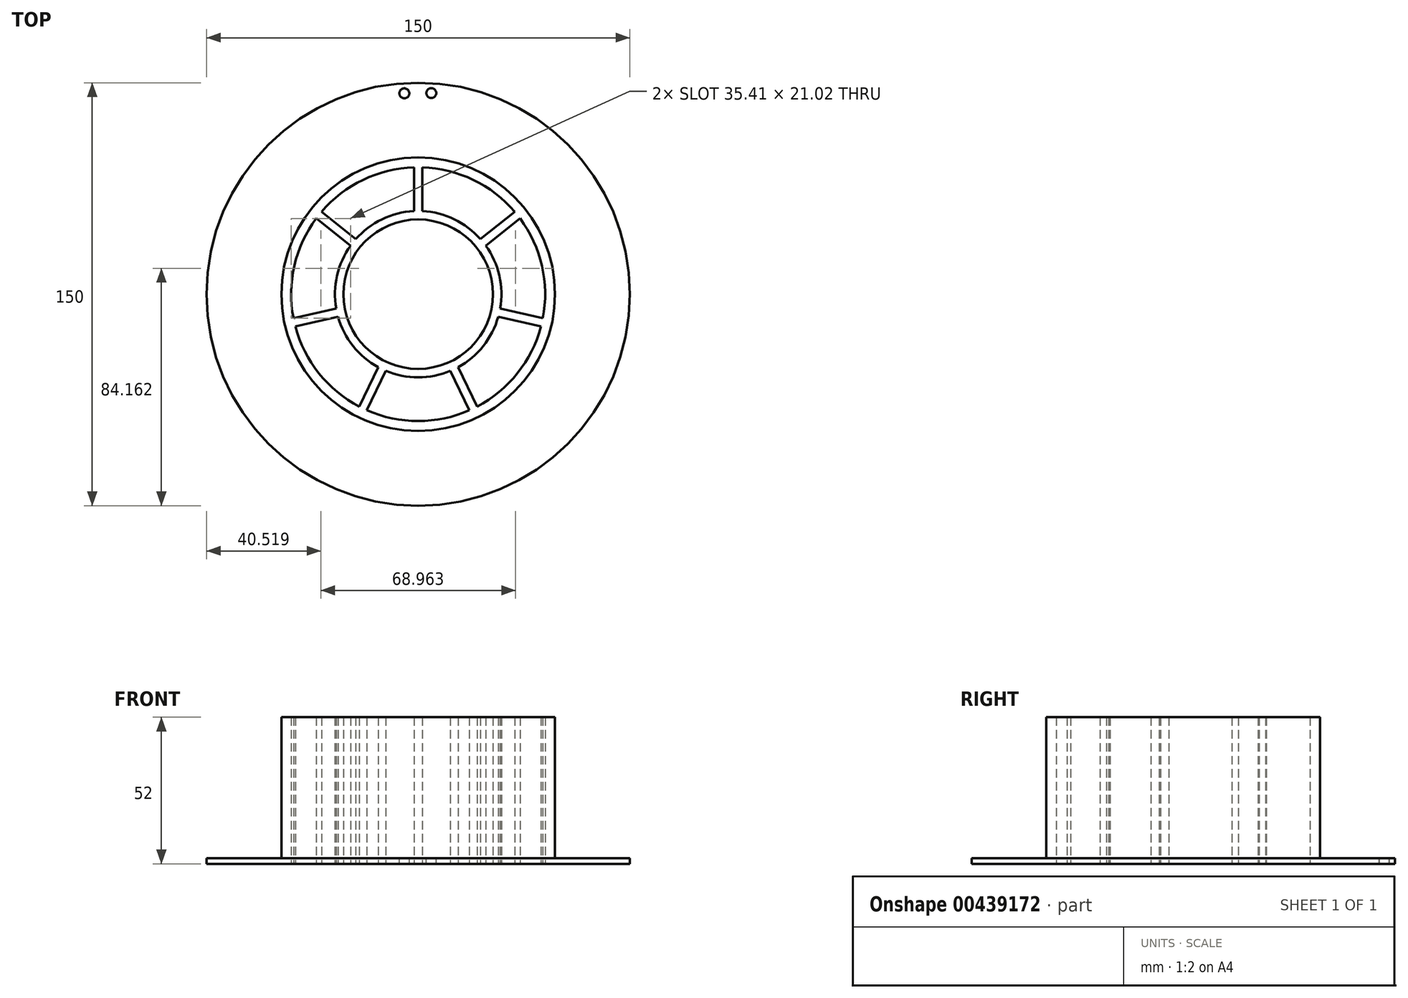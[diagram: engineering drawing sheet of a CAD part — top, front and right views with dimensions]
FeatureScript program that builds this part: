
annotation { "Feature Type Name" : "Feature", "Feature Type Description" : "" }
export const myFeature = defineFeature(function(context is Context, id is Id, definition is map)
    precondition{}
    {
        {
            var Q0;
            Q0=qCreatedBy(makeId("Top.planeOp"),FACE);
            var sketch = newSketch(context, id + "F0", { "sketchPlane" : qUnion([Q0])});
            skCircle(sketch, "E0", {"center": v(0, 0) * mm, "radius": 26.5 * mm});
            skArc(sketch, "E1", {"start": v(-1.5, 29.46) * mm, "mid": v(-12.8, 26.58) * mm, "end": v(-22.1, 19.54) * mm});
            skArc(sketch, "E2", {"start": v(-1.5, 44.97) * mm, "mid": v(-19.52, 40.54) * mm, "end": v(-34.23, 29.21) * mm});
            skCircle(sketch, "E3", {"center": v(0, 0) * mm, "radius": 75 * mm});
            skLineSegment(sketch, "E4", {"start": v(-1.5, 29.46) * mm, "end": v(-1.5, 44.97) * mm});
            skLineSegment(sketch, "E5", {"start": v(1.5, 29.46) * mm, "end": v(1.5, 44.97) * mm});
            skLineSegment(sketch, "E6.1.0", {"start": v(-23.97, 17.2) * mm, "end": v(-36.1, 26.87) * mm});
            skLineSegment(sketch, "E6.1.1", {"start": v(-22.1, 19.54) * mm, "end": v(-34.23, 29.21) * mm});
            skLineSegment(sketch, "E6.2.0", {"start": v(-28.39, -8.02) * mm, "end": v(-43.51, -11.47) * mm});
            skLineSegment(sketch, "E6.2.1", {"start": v(-29.06, -5.1) * mm, "end": v(-44.18, -8.55) * mm});
            skLineSegment(sketch, "E6.3.0", {"start": v(-11.43, -27.2) * mm, "end": v(-18.16, -41.17) * mm});
            skLineSegment(sketch, "E6.3.1", {"start": v(-14.13, -25.9) * mm, "end": v(-20.87, -39.87) * mm});
            skLineSegment(sketch, "E6.4.0", {"start": v(14.13, -25.9) * mm, "end": v(20.87, -39.87) * mm});
            skLineSegment(sketch, "E6.4.1", {"start": v(11.43, -27.2) * mm, "end": v(18.16, -41.17) * mm});
            skLineSegment(sketch, "E6.5.0", {"start": v(29.06, -5.1) * mm, "end": v(44.18, -8.55) * mm});
            skLineSegment(sketch, "E6.5.1", {"start": v(28.39, -8.02) * mm, "end": v(43.51, -11.47) * mm});
            skLineSegment(sketch, "E6.6.0", {"start": v(22.1, 19.54) * mm, "end": v(34.23, 29.21) * mm});
            skLineSegment(sketch, "E6.6.1", {"start": v(23.97, 17.2) * mm, "end": v(36.1, 26.87) * mm});
            skLineSegment(sketch, "E6.anchor1", {"start": v(0, 0) * mm, "end": v(-1.5, 29.46) * mm, "construction": true});
            skLineSegment(sketch, "E6.anchor2", {"start": v(0, 0) * mm, "end": v(-1.5, 29.46) * mm, "construction": true});
            skArc(sketch, "E7.trimOffspring", {"start": v(-36.1, 26.87) * mm, "mid": v(-43.87, 10.01) * mm, "end": v(-44.18, -8.55) * mm});
            skArc(sketch, "E8.trimOffspring", {"start": v(-23.97, 17.2) * mm, "mid": v(-28.76, 6.56) * mm, "end": v(-29.06, -5.1) * mm});
            skArc(sketch, "E9.trimOffspring", {"start": v(-28.39, -8.02) * mm, "mid": v(-23.06, -18.4) * mm, "end": v(-14.13, -25.9) * mm});
            skArc(sketch, "E10.trimOffspring", {"start": v(-43.51, -11.47) * mm, "mid": v(-35.18, -28.06) * mm, "end": v(-20.87, -39.87) * mm});
            skArc(sketch, "E11.trimOffspring", {"start": v(-11.43, -27.2) * mm, "mid": v(0, -29.5) * mm, "end": v(11.43, -27.2) * mm});
            skArc(sketch, "E12.trimOffspring", {"start": v(-18.16, -41.17) * mm, "mid": v(0, -45) * mm, "end": v(18.16, -41.17) * mm});
            skArc(sketch, "E13.trimOffspring", {"start": v(14.13, -25.9) * mm, "mid": v(23.06, -18.4) * mm, "end": v(28.39, -8.02) * mm});
            skArc(sketch, "E14.trimOffspring", {"start": v(20.87, -39.87) * mm, "mid": v(35.18, -28.06) * mm, "end": v(43.51, -11.47) * mm});
            skArc(sketch, "E15.trimOffspring", {"start": v(44.18, -8.55) * mm, "mid": v(43.87, 10.01) * mm, "end": v(36.1, 26.87) * mm});
            skArc(sketch, "E16.trimOffspring", {"start": v(29.06, -5.1) * mm, "mid": v(28.76, 6.56) * mm, "end": v(23.97, 17.2) * mm});
            skArc(sketch, "E17.trimOffspring", {"start": v(34.23, 29.21) * mm, "mid": v(19.52, 40.54) * mm, "end": v(1.5, 44.97) * mm});
            skArc(sketch, "E18.trimOffspring", {"start": v(22.1, 19.54) * mm, "mid": v(12.8, 26.58) * mm, "end": v(1.5, 29.46) * mm});
            skSolve(sketch);
        }
        {
            var Q0;
            Q0=makeQuery(id+"F0.imprint","IMPRINT",FACE,{"disambiguationData":[TD([[makeQuery(id+"F0.imprint","IMPRINT",EDGE,{"derivedFrom":sQuery(id+"F0.wireOp",EDGE,"E0")}),-1.0]])]});
            extrude(context, id + "F1", {"entities" : qUnion([Q0]), "depth" : 2 * mm});
        }
        {
            var Q0;
            Q0=makeQuery(id+"F1.opExtrude","CAP_FACE",FACE,{"disambiguationData":[OSD([sQuery(id+"F0.wireOp",EDGE,"E0"),sQuery(id+"F0.wireOp",EDGE,"E1"),sQuery(id+"F0.wireOp",EDGE,"E2"),sQuery(id+"F0.wireOp",EDGE,"E3"),sQuery(id+"F0.wireOp",EDGE,"E6.1.0"),sQuery(id+"F0.wireOp",EDGE,"E6.1.1"),sQuery(id+"F0.wireOp",EDGE,"E6.2.0"),sQuery(id+"F0.wireOp",EDGE,"E6.2.1"),sQuery(id+"F0.wireOp",EDGE,"E6.3.0"),sQuery(id+"F0.wireOp",EDGE,"E6.3.1"),sQuery(id+"F0.wireOp",EDGE,"E6.4.0"),sQuery(id+"F0.wireOp",EDGE,"E6.4.1"),sQuery(id+"F0.wireOp",EDGE,"E6.5.0"),sQuery(id+"F0.wireOp",EDGE,"E6.5.1"),sQuery(id+"F0.wireOp",EDGE,"E6.6.0"),sQuery(id+"F0.wireOp",EDGE,"E6.6.1"),sQuery(id+"F0.wireOp",EDGE,"E4"),sQuery(id+"F0.wireOp",EDGE,"E5"),sQuery(id+"F0.wireOp",EDGE,"E7.trimOffspring"),sQuery(id+"F0.wireOp",EDGE,"E8.trimOffspring"),sQuery(id+"F0.wireOp",EDGE,"E9.trimOffspring"),sQuery(id+"F0.wireOp",EDGE,"E10.trimOffspring"),sQuery(id+"F0.wireOp",EDGE,"E11.trimOffspring"),sQuery(id+"F0.wireOp",EDGE,"E12.trimOffspring"),sQuery(id+"F0.wireOp",EDGE,"E13.trimOffspring"),sQuery(id+"F0.wireOp",EDGE,"E14.trimOffspring"),sQuery(id+"F0.wireOp",EDGE,"E15.trimOffspring"),sQuery(id+"F0.wireOp",EDGE,"E16.trimOffspring"),sQuery(id+"F0.wireOp",EDGE,"E17.trimOffspring"),sQuery(id+"F0.wireOp",EDGE,"E18.trimOffspring")])],"isStart":false});
            var sketch = newSketch(context, id + "F2", { "sketchPlane" : qUnion([Q0])});
            skCircle(sketch, "E19", {"center": v(0, 0) * mm, "radius": 48.5 * mm});
            skSolve(sketch);
        }
        {
            var Q0;
            Q0=makeQuery(id+"F2.imprint","IMPRINT",FACE,{"disambiguationData":[TD([[makeQuery(id+"F2.imprint","IMPRINT",EDGE,{"derivedFrom":sQuery(id+"F2.wireOp",EDGE,"E19")}),1.0]])]});
            extrude(context, id + "F3", {"entities" : qUnion([Q0]), "operationType" : NewBodyOperationType.ADD, "depth" : 50 * mm});
        }
        {
            var Q0;
            Q0=makeQuery(id+"F1.opExtrude","CAP_FACE",FACE,{"disambiguationData":[OSD([sQuery(id+"F0.wireOp",EDGE,"E0"),sQuery(id+"F0.wireOp",EDGE,"E1"),sQuery(id+"F0.wireOp",EDGE,"E2"),sQuery(id+"F0.wireOp",EDGE,"E3"),sQuery(id+"F0.wireOp",EDGE,"E6.1.0"),sQuery(id+"F0.wireOp",EDGE,"E6.1.1"),sQuery(id+"F0.wireOp",EDGE,"E6.2.0"),sQuery(id+"F0.wireOp",EDGE,"E6.2.1"),sQuery(id+"F0.wireOp",EDGE,"E6.3.0"),sQuery(id+"F0.wireOp",EDGE,"E6.3.1"),sQuery(id+"F0.wireOp",EDGE,"E6.4.0"),sQuery(id+"F0.wireOp",EDGE,"E6.4.1"),sQuery(id+"F0.wireOp",EDGE,"E6.5.0"),sQuery(id+"F0.wireOp",EDGE,"E6.5.1"),sQuery(id+"F0.wireOp",EDGE,"E6.6.0"),sQuery(id+"F0.wireOp",EDGE,"E6.6.1"),sQuery(id+"F0.wireOp",EDGE,"E4"),sQuery(id+"F0.wireOp",EDGE,"E5"),sQuery(id+"F0.wireOp",EDGE,"E7.trimOffspring"),sQuery(id+"F0.wireOp",EDGE,"E8.trimOffspring"),sQuery(id+"F0.wireOp",EDGE,"E9.trimOffspring"),sQuery(id+"F0.wireOp",EDGE,"E10.trimOffspring"),sQuery(id+"F0.wireOp",EDGE,"E11.trimOffspring"),sQuery(id+"F0.wireOp",EDGE,"E12.trimOffspring"),sQuery(id+"F0.wireOp",EDGE,"E13.trimOffspring"),sQuery(id+"F0.wireOp",EDGE,"E14.trimOffspring"),sQuery(id+"F0.wireOp",EDGE,"E15.trimOffspring"),sQuery(id+"F0.wireOp",EDGE,"E16.trimOffspring"),sQuery(id+"F0.wireOp",EDGE,"E17.trimOffspring"),sQuery(id+"F0.wireOp",EDGE,"E18.trimOffspring")])],"isStart":false});
            var sketch = newSketch(context, id + "F4", { "sketchPlane" : qUnion([Q0])});
            skCircle(sketch, "E20", {"center": v(-4.9, 71.23) * mm, "radius": 1.75 * mm});
            skCircle(sketch, "E21", {"center": v(4.65, 71.3) * mm, "radius": 1.75 * mm});
            skSolve(sketch);
        }
        {
            var Q0;
            Q0=makeQuery(id+"F4.imprint","IMPRINT",FACE,{"disambiguationData":[TD([[makeQuery(id+"F4.imprint","IMPRINT",EDGE,{"derivedFrom":sQuery(id+"F4.wireOp",EDGE,"E20")}),1.0]])]});
            var Q1;
            Q1=makeQuery(id+"F4.imprint","IMPRINT",FACE,{"disambiguationData":[TD([[makeQuery(id+"F4.imprint","IMPRINT",EDGE,{"derivedFrom":sQuery(id+"F4.wireOp",EDGE,"E21")}),1.0]])]});
            extrude(context, id + "F5", {"entities" : qUnion([Q0, Q1]), "operationType" : NewBodyOperationType.REMOVE, "endBound" : BoundingType.THROUGH_ALL, "oppositeDirection" : true, "depth" : 25 * mm});
        }
    });
